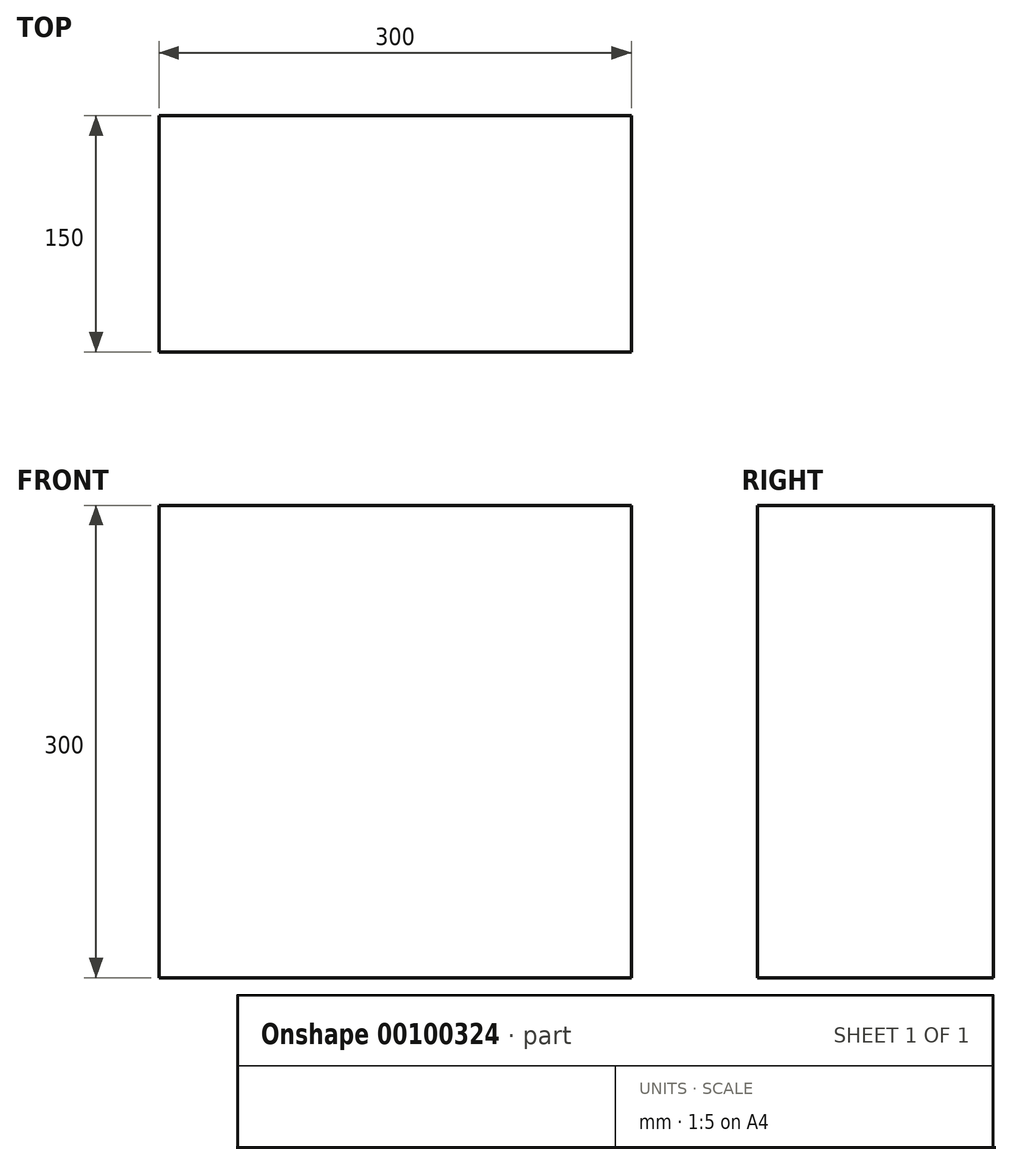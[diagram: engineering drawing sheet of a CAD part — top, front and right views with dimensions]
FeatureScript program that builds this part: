
annotation { "Feature Type Name" : "Feature", "Feature Type Description" : "" }
export const myFeature = defineFeature(function(context is Context, id is Id, definition is map)
    precondition{}
    {
        {
            var Q0;
            Q0=qCreatedBy(makeId("Top.planeOp"),FACE);
            var sketch = newSketch(context, id + "F0", { "sketchPlane" : qUnion([Q0])});
            skLineSegment(sketch, "E0.bottom", {"start": v(-152.14, 15.79) * mm, "end": v(147.86, 15.79) * mm});
            skLineSegment(sketch, "E0.top", {"start": v(-152.14, -134.21) * mm, "end": v(147.86, -134.21) * mm});
            skLineSegment(sketch, "E0.left", {"start": v(-152.14, 15.79) * mm, "end": v(-152.14, -134.21) * mm});
            skLineSegment(sketch, "E0.right", {"start": v(147.86, 15.79) * mm, "end": v(147.86, -134.21) * mm});
            skSolve(sketch);
        }
        {
            var Q0;
            Q0 = qSketchRegion(id + "F0", true);
            extrude(context, id + "F1", {"entities" : qUnion([Q0]), "depth" : 300 * mm});
        }
    });
